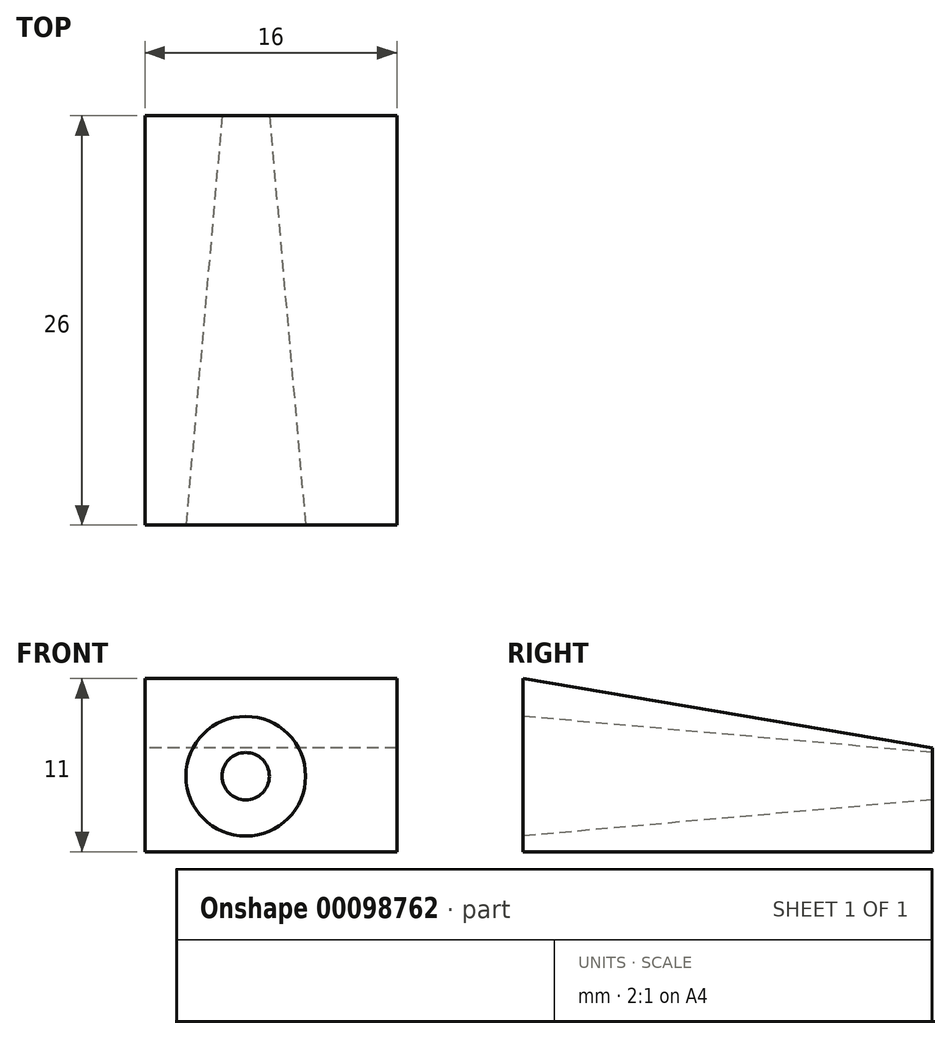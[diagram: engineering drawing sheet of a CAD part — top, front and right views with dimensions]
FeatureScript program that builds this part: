
annotation { "Feature Type Name" : "Feature", "Feature Type Description" : "" }
export const myFeature = defineFeature(function(context is Context, id is Id, definition is map)
    precondition{}
    {
        {
            var Q0;
            Q0=qCreatedBy(makeId("Front.planeOp"),FACE);
            var sketch = newSketch(context, id + "F0", { "sketchPlane" : qUnion([Q0])});
            skLineSegment(sketch, "E0.bottom", {"start": v(-8, 5.5) * mm, "end": v(8, 5.5) * mm});
            skLineSegment(sketch, "E0.top", {"start": v(-8, -5.5) * mm, "end": v(8, -5.5) * mm});
            skLineSegment(sketch, "E0.left", {"start": v(-8, 5.5) * mm, "end": v(-8, -5.5) * mm});
            skLineSegment(sketch, "E0.right", {"start": v(8, 5.5) * mm, "end": v(8, -5.5) * mm});
            skPoint(sketch, "E0.middle", {"position": v(0, 0) * mm});
            skSolve(sketch);
        }
        {
            var Q0;
            Q0 = qSketchRegion(id + "F0", true);
            extrude(context, id + "F1", {"entities" : qUnion([Q0]), "oppositeDirection" : true, "depth" : 26 * mm});
        }
        {
            var Q0;
            Q0=makeQuery(id+"F1.opExtrude","SWEPT_FACE",FACE,{"disambiguationData":[OSD([sQuery(id+"F0.wireOp",EDGE,"E0.left")])]});
            var sketch = newSketch(context, id + "F2", { "sketchPlane" : qUnion([Q0])});
            skPoint(sketch, "E1", {"position": v(-26, 1.1) * mm});
            skLineSegment(sketch, "E2", {"start": v(-26, 1.1) * mm, "end": v(0, 5.5) * mm});
            skSolve(sketch);
        }
        {
            var Q0;
            {var subQ0=sQuery(id+"F2.wireOp",EDGE,"E2");Q0=makeQuery(id+"F2.imprint","IMPRINT",FACE,{"disambiguationData":[TD([[makeQuery(id+"F2.imprint","IMPRINT",EDGE,{"derivedFrom":subQ0}),-1.0]])]});}
            cPlane(context, id + "F3", {"entities" : qUnion([Q0]), "cplaneType" : CPlaneType.OFFSET, "offset" : 6.4 * mm, "oppositeDirection" : true, "width" : 150 * mm, "height" : 150 * mm});
        }
        {
            var Q0;
            Q0=qCreatedBy(id+"F3.planeOp",FACE);
            var sketch = newSketch(context, id + "F4", { "sketchPlane" : qUnion([Q0])});
            skLineSegment(sketch, "E3", {"start": v(0, -0.7) * mm, "end": v(-26, -0.7) * mm});
            skLineSegment(sketch, "E4", {"start": v(0, -0.7) * mm, "end": v(0, 3.1) * mm});
            skLineSegment(sketch, "E5", {"start": v(-26, -0.7) * mm, "end": v(-26, 0.8) * mm});
            skLineSegment(sketch, "E6", {"start": v(-26, 0.8) * mm, "end": v(0, 3.1) * mm});
            skSolve(sketch);
        }
        {
            var Q0;
            Q0 = qSketchRegion(id + "F4", true);
            var Q1;
            Q1=sQuery(id+"F4.wireOp",EDGE,"E3");
            revolve(context, id + "F5", {"operationType" : NewBodyOperationType.REMOVE, "entities" : qUnion([Q0]), "axis" : qUnion([Q1]), "revolveType" : RevolveType.FULL, "oppositeDirection" : true});
        }
        {
            var Q0;
            {var subQ0=sQuery(id+"F2.wireOp",EDGE,"E2");Q0=makeQuery(id+"F2.imprint","IMPRINT",FACE,{"disambiguationData":[TD([[makeQuery(id+"F2.imprint","IMPRINT",EDGE,{"derivedFrom":subQ0}),1.0]])]});}
            extrude(context, id + "F6", {"entities" : qUnion([Q0]), "operationType" : NewBodyOperationType.REMOVE, "oppositeDirection" : true, "depth" : 19.83 * mm});
        }
    });
